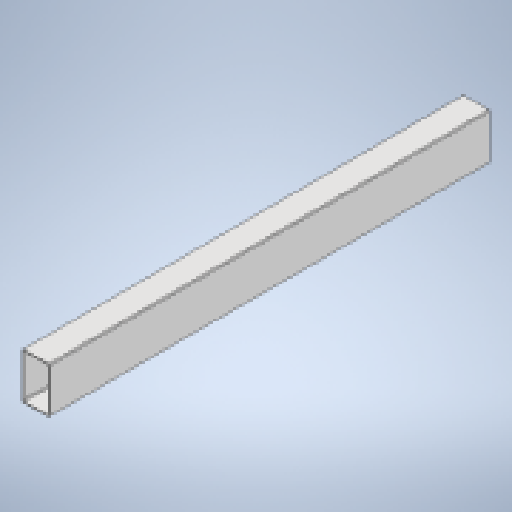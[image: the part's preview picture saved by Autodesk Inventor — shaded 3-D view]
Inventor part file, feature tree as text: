
AUTODESK INVENTOR PART (.ipt)
format: ipt  version: 2023 (Build 270158000, 158)  size: 180,736 bytes
history: native  units: in
note: dims shown in document units (in); Inventor stores cm internally (conversion verified against a paired STEP export)
features: extrude x2, sketch x2, shell x1, fillet x1
ambient origin geometry x8: Origin, YZ Plane, XZ Plane, XY Plane, X Axis, Y Axis, Z Axis, Center Point
bodies: Solid1 (feature_tree)
feature tree (6):
  extrude  "Extrusion1"  Depth=5.0in
  shell  "Shell1"  Thickness=49.0in
  fillet  "Fillet1"  Radius=0.125in
  extrude  "Extrusion2"  Depth=3.0in
  sketch  "Sketch1"  dims[d0=3.0in d1=5.0in d2=49.0in d3=0.0in d4=0.125in]
  sketch  "Sketch2"  dims[d5=0.125in d6=3.0in d7=3.0in d8=2.0866in d9=1.5748in d10=0.315in d11=0.7874in d13=46.0in d14=0.3937in d16=1.0in d18=49.0in d19=0.0in]
